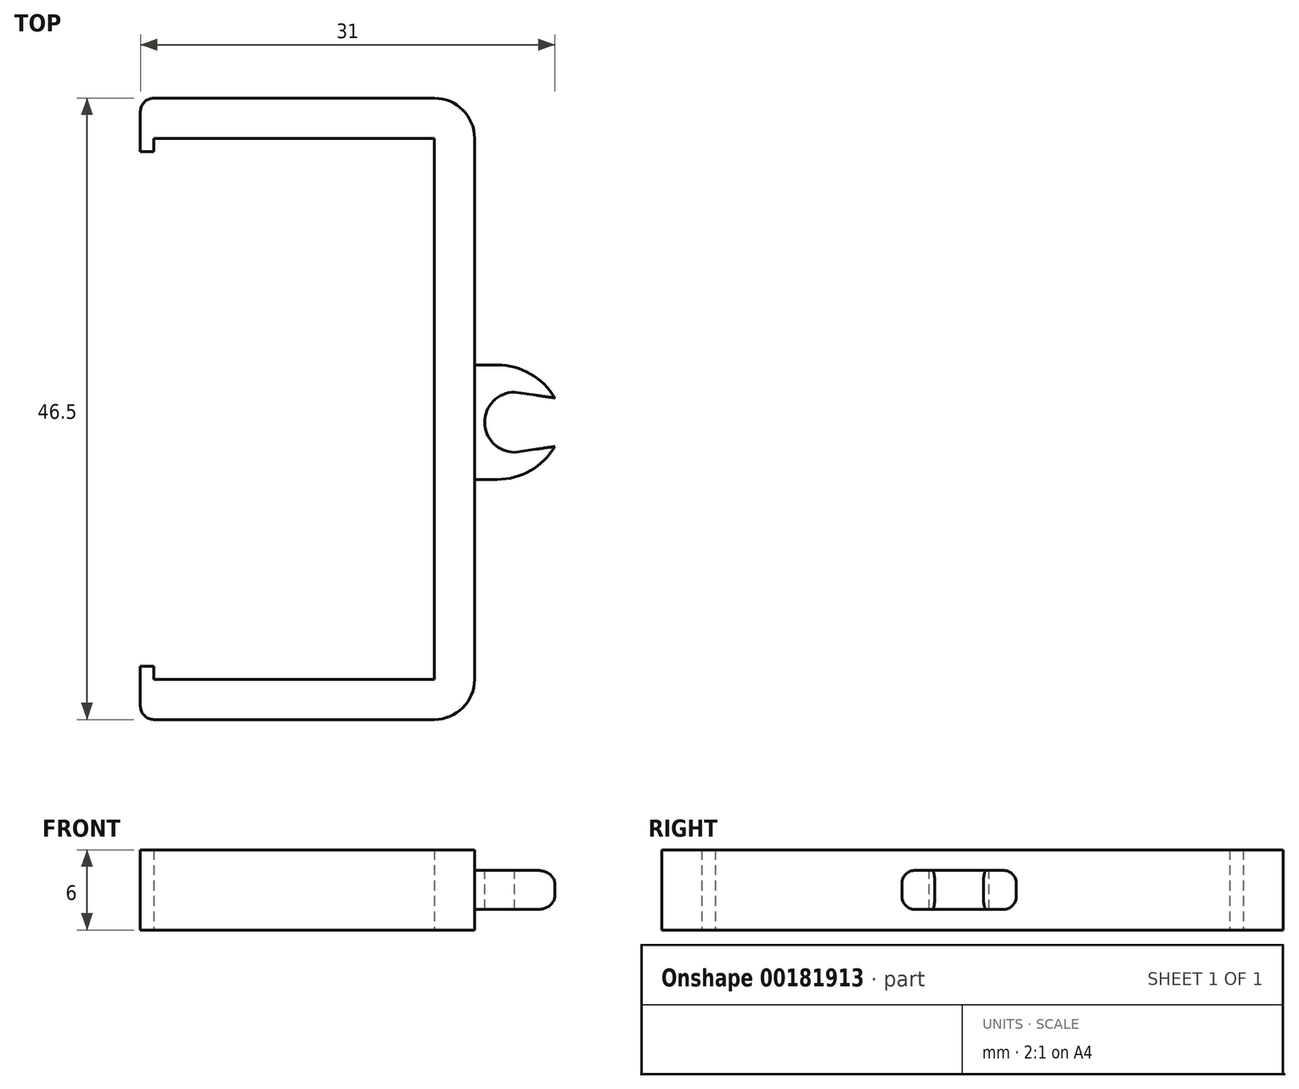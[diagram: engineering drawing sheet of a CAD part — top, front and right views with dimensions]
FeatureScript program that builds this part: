
annotation { "Feature Type Name" : "Feature", "Feature Type Description" : "" }
export const myFeature = defineFeature(function(context is Context, id is Id, definition is map)
    precondition{}
    {
        {
            var Q0;
            Q0=qCreatedBy(makeId("Top.planeOp"),FACE);
            var sketch = newSketch(context, id + "F0", { "sketchPlane" : qUnion([Q0])});
            skLineSegment(sketch, "E0", {"start": v(16.58, 28.27) * mm, "end": v(16.58, -12.23) * mm});
            skLineSegment(sketch, "E1", {"start": v(16.58, 28.27) * mm, "end": v(-4.42, 28.27) * mm});
            skLineSegment(sketch, "E2", {"start": v(16.58, -12.23) * mm, "end": v(-4.42, -12.23) * mm});
            skLineSegment(sketch, "E3", {"start": v(-4.42, -12.23) * mm, "end": v(-4.42, -11.23) * mm});
            skLineSegment(sketch, "E4", {"start": v(-4.42, 28.27) * mm, "end": v(-4.42, 27.27) * mm});
            skLineSegment(sketch, "E5.0", {"start": v(-5.42, 27.27) * mm, "end": v(-5.42, 27.27) * mm});
            skLineSegment(sketch, "E6.0", {"start": v(-5.42, -13.23) * mm, "end": v(-5.42, -11.23) * mm});
            skLineSegment(sketch, "E7.0", {"start": v(16.58, -15.23) * mm, "end": v(-4.42, -15.23) * mm});
            skLineSegment(sketch, "E8.0", {"start": v(16.58, 31.27) * mm, "end": v(-4.42, 31.27) * mm});
            skLineSegment(sketch, "E9.0", {"start": v(19.58, 27.27) * mm, "end": v(19.58, -13.23) * mm});
            skLineSegment(sketch, "E10", {"start": v(-5.42, 27.27) * mm, "end": v(-5.42, 31.27) * mm});
            skLineSegment(sketch, "E11", {"start": v(-4.42, 31.27) * mm, "end": v(-5.42, 31.27) * mm});
            skLineSegment(sketch, "E12", {"start": v(16.58, 31.27) * mm, "end": v(19.58, 31.27) * mm});
            skLineSegment(sketch, "E13", {"start": v(19.58, 27.27) * mm, "end": v(19.58, 31.27) * mm});
            skLineSegment(sketch, "E14", {"start": v(-4.42, 27.27) * mm, "end": v(-5.42, 27.27) * mm});
            skLineSegment(sketch, "E15", {"start": v(19.58, -13.23) * mm, "end": v(19.58, -15.23) * mm});
            skLineSegment(sketch, "E16", {"start": v(16.58, -15.23) * mm, "end": v(19.58, -15.23) * mm});
            skLineSegment(sketch, "E17", {"start": v(-5.42, -13.23) * mm, "end": v(-5.42, -15.23) * mm});
            skLineSegment(sketch, "E18", {"start": v(-4.42, -15.23) * mm, "end": v(-5.42, -15.23) * mm});
            skLineSegment(sketch, "E19", {"start": v(-4.42, -11.23) * mm, "end": v(-5.42, -11.23) * mm});
            skSolve(sketch);
        }
        {
            var Q0;
            Q0=makeQuery(id+"F0.imprint","IMPRINT",FACE,{"disambiguationData":[TD([[makeQuery(id+"F0.imprint","IMPRINT",EDGE,{"derivedFrom":sQuery(id+"F0.wireOp",EDGE,"E0")}),1.0]])]});
            extrude(context, id + "F1", {"entities" : qUnion([Q0]), "depth" : 6 * mm});
        }
        {
            var Q0;
            Q0=makeQuery(id+"F1.opExtrude","SWEPT_FACE",FACE,{"disambiguationData":[OSD([sQuery(id+"F0.wireOp",EDGE,"E9.0"),sQuery(id+"F0.wireOp",EDGE,"E13"),sQuery(id+"F0.wireOp",EDGE,"E15")])]});
            var sketch = newSketch(context, id + "F2", { "sketchPlane" : qUnion([Q0])});
            skPoint(sketch, "E20.endSnap0", {"position": v(8.02, 6) * mm});
            skLineSegment(sketch, "E21.bottom", {"start": v(2.73, 4.47) * mm, "end": v(11.3, 4.47) * mm});
            skLineSegment(sketch, "E21.top", {"start": v(2.73, 1.53) * mm, "end": v(11.3, 1.53) * mm});
            skLineSegment(sketch, "E21.left", {"start": v(2.73, 4.47) * mm, "end": v(2.73, 1.53) * mm});
            skLineSegment(sketch, "E21.right", {"start": v(11.3, 4.47) * mm, "end": v(11.3, 1.53) * mm});
            skSolve(sketch);
        }
        {
            var Q0;
            Q0 = qSketchRegion(id + "F2", true);
            extrude(context, id + "F3", {"entities" : qUnion([Q0]), "operationType" : NewBodyOperationType.ADD, "depth" : 6 * mm});
        }
        {
            var Q0;
            Q0=makeQuery(id+"F3.opExtrude","SWEPT_FACE",FACE,{"disambiguationData":[OSD([sQuery(id+"F2.wireOp",EDGE,"E21.bottom")])]});
            var sketch = newSketch(context, id + "F4", { "sketchPlane" : qUnion([Q0])});
            skLineSegment(sketch, "E22", {"start": v(22.58, 11.3) * mm, "end": v(22.58, 2.73) * mm, "construction": true});
            skArc(sketch, "E23", {"start": v(22.58, 9.27) * mm, "mid": v(20.33, 7.02) * mm, "end": v(22.58, 4.77) * mm});
            skLineSegment(sketch, "E24", {"start": v(25.58, 8.83) * mm, "end": v(22.58, 9.27) * mm});
            skLineSegment(sketch, "E25.MirrorCS", {"start": v(25.58, 5.2) * mm, "end": v(22.58, 4.77) * mm});
            skLineSegment(sketch, "E26", {"start": v(25.58, 8.83) * mm, "end": v(25.58, 5.2) * mm});
            skSolve(sketch);
        }
        {
            var Q0;
            Q0=makeQuery(id+"F4.imprint","IMPRINT",FACE,{"disambiguationData":[TD([[makeQuery(id+"F4.imprint","IMPRINT",EDGE,{"derivedFrom":sQuery(id+"F4.wireOp",EDGE,"E23")}),1.0]])]});
            var Q1;
            Q1=sQuery(id+"F4.wireOp",EDGE,"E24");
            var Q2;
            Q2=sQuery(id+"F4.wireOp",EDGE,"E23");
            var Q3;
            Q3=sQuery(id+"F4.wireOp",EDGE,"C4R9Oy1y-7e1z-FXny-91y1-kyaZ4qe8YO9C");
            var Q4;
            Q4=sQuery(id+"F4.wireOp",EDGE,"JZYNILZq-mjDS-Zgyg-Tk2O-Pl40O7umI2Ae");
            extrude(context, id + "F5", {"entities" : qUnion([Q0]), "operationType" : NewBodyOperationType.REMOVE, "surfaceEntities" : qUnion([Q1, Q2, Q3, Q4]), "oppositeDirection" : true, "depth" : 25 * mm});
        }
        {
            var Q0;
            Q0=makeQuery(id+"F3.opExtrude","CAP_EDGE",EDGE,{"disambiguationData":[OSD([sQuery(id+"F2.wireOp",EDGE,"E21.left")])],"isStart":false});
            var Q1;
            Q1=makeQuery(id+"F3.opExtrude","CAP_EDGE",EDGE,{"disambiguationData":[OSD([sQuery(id+"F2.wireOp",EDGE,"E21.right")])],"isStart":false});
            fillet(context, id + "F6", {"entities" : qUnion([Q0, Q1]), "radius" : 5 * mm, "tangentPropagation" : true, "allowEdgeOverflow" : false});
        }
        {
            var Q0;
            Q0=makeQuery(id+"F1.opExtrude","SWEPT_EDGE",EDGE,{"disambiguationData":[OSD([sQuery(id+"F0.wireOp",EDGE,"E15"),sQuery(id+"F0.wireOp",EDGE,"E16")])]});
            var Q1;
            Q1=makeQuery(id+"F1.opExtrude","SWEPT_EDGE",EDGE,{"disambiguationData":[OSD([sQuery(id+"F0.wireOp",EDGE,"E12"),sQuery(id+"F0.wireOp",EDGE,"E13")])]});
            fillet(context, id + "F7", {"entities" : qUnion([Q0, Q1]), "radius" : 3 * mm, "tangentPropagation" : true, "allowEdgeOverflow" : false});
        }
        {
            var Q0;
            Q0=makeQuery(id+"F1.opExtrude","SWEPT_EDGE",EDGE,{"disambiguationData":[OSD([sQuery(id+"F0.wireOp",EDGE,"E17"),sQuery(id+"F0.wireOp",EDGE,"E18")])]});
            var Q1;
            Q1=makeQuery(id+"F1.opExtrude","SWEPT_EDGE",EDGE,{"disambiguationData":[OSD([sQuery(id+"F0.wireOp",EDGE,"E10"),sQuery(id+"F0.wireOp",EDGE,"E11")])]});
            var Q2;
            Q2=makeQuery(id+"F6.opFillet","BLEND_EDGE",EDGE,{"blendedFrom":[makeQuery(id+"F3.opExtrude","CAP_EDGE",EDGE,{"disambiguationData":[OSD([sQuery(id+"F2.wireOp",EDGE,"E21.left")])],"isStart":false}),makeQuery(id+"F3.opExtrude","SWEPT_FACE",FACE,{"disambiguationData":[OSD([sQuery(id+"F2.wireOp",EDGE,"E21.bottom")])]})],"blendedInto":[makeQuery(id+"F3.opExtrude","SWEPT_FACE",FACE,{"disambiguationData":[OSD([sQuery(id+"F2.wireOp",EDGE,"E21.bottom")])]})]});
            var Q3;
            Q3=makeQuery(id+"F6.opFillet","BLEND_EDGE",EDGE,{"blendedFrom":[makeQuery(id+"F3.opExtrude","CAP_EDGE",EDGE,{"disambiguationData":[OSD([sQuery(id+"F2.wireOp",EDGE,"E21.left")])],"isStart":false}),makeQuery(id+"F3.opExtrude","SWEPT_FACE",FACE,{"disambiguationData":[OSD([sQuery(id+"F2.wireOp",EDGE,"E21.top")])]})],"blendedInto":[makeQuery(id+"F3.opExtrude","SWEPT_FACE",FACE,{"disambiguationData":[OSD([sQuery(id+"F2.wireOp",EDGE,"E21.top")])]})]});
            var Q4;
            Q4=makeQuery(id+"F6.opFillet","BLEND_EDGE",EDGE,{"blendedFrom":[makeQuery(id+"F3.opExtrude","CAP_EDGE",EDGE,{"disambiguationData":[OSD([sQuery(id+"F2.wireOp",EDGE,"E21.right")])],"isStart":false}),makeQuery(id+"F3.opExtrude","SWEPT_FACE",FACE,{"disambiguationData":[OSD([sQuery(id+"F2.wireOp",EDGE,"E21.top")])]})],"blendedInto":[makeQuery(id+"F3.opExtrude","SWEPT_FACE",FACE,{"disambiguationData":[OSD([sQuery(id+"F2.wireOp",EDGE,"E21.top")])]})]});
            var Q5;
            Q5=makeQuery(id+"F6.opFillet","BLEND_EDGE",EDGE,{"blendedFrom":[makeQuery(id+"F3.opExtrude","CAP_EDGE",EDGE,{"disambiguationData":[OSD([sQuery(id+"F2.wireOp",EDGE,"E21.right")])],"isStart":false}),makeQuery(id+"F3.opExtrude","SWEPT_FACE",FACE,{"disambiguationData":[OSD([sQuery(id+"F2.wireOp",EDGE,"E21.bottom")])]})],"blendedInto":[makeQuery(id+"F3.opExtrude","SWEPT_FACE",FACE,{"disambiguationData":[OSD([sQuery(id+"F2.wireOp",EDGE,"E21.bottom")])]})]});
            fillet(context, id + "F8", {"entities" : qUnion([Q0, Q1, Q2, Q3, Q4, Q5]), "radius" : 1 * mm, "tangentPropagation" : true, "allowEdgeOverflow" : false});
        }
    });
